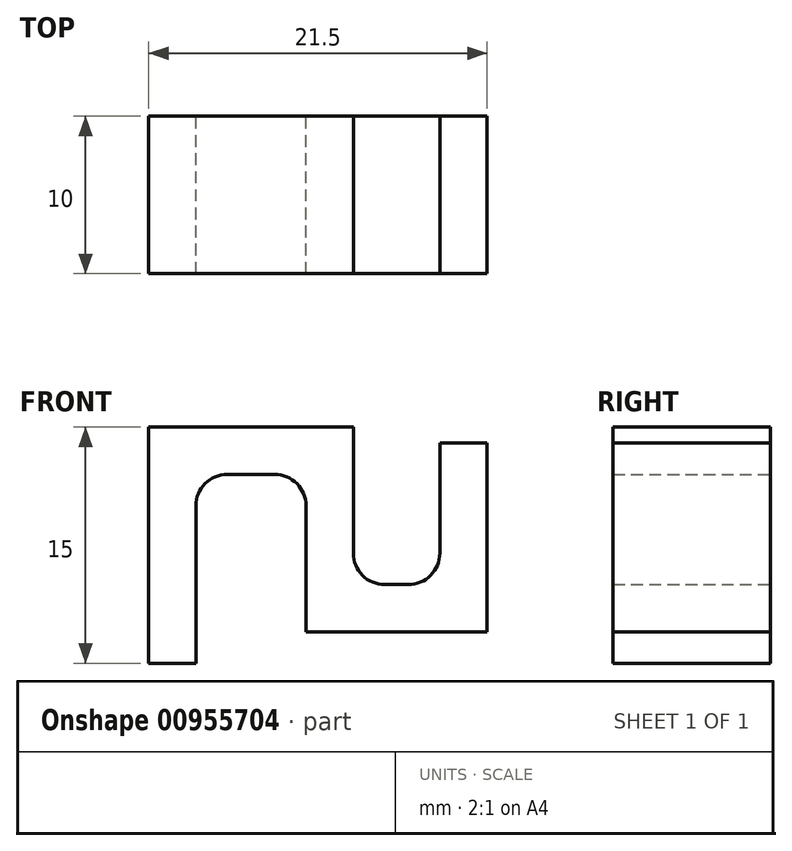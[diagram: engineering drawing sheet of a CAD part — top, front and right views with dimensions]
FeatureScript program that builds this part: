
annotation { "Feature Type Name" : "Feature", "Feature Type Description" : "" }
export const myFeature = defineFeature(function(context is Context, id is Id, definition is map)
    precondition{}
    {
        {
            var Q0;
            Q0=qCreatedBy(makeId("Front.planeOp"),FACE);
            var sketch = newSketch(context, id + "F0", { "sketchPlane" : qUnion([Q0])});
            skLineSegment(sketch, "E0", {"start": v(0, 0) * mm, "end": v(0, 15) * mm});
            skLineSegment(sketch, "E1", {"start": v(0, 15) * mm, "end": v(13, 15) * mm});
            skLineSegment(sketch, "E2", {"start": v(13, 15) * mm, "end": v(13, 7) * mm});
            skLineSegment(sketch, "E3", {"start": v(15, 5) * mm, "end": v(16.5, 5) * mm});
            skLineSegment(sketch, "E4", {"start": v(18.5, 7) * mm, "end": v(18.5, 14) * mm});
            skLineSegment(sketch, "E5", {"start": v(18.5, 14) * mm, "end": v(21.5, 14) * mm});
            skLineSegment(sketch, "E6", {"start": v(21.5, 14) * mm, "end": v(21.5, 2) * mm});
            skLineSegment(sketch, "E7", {"start": v(21.5, 2) * mm, "end": v(10, 2) * mm});
            skLineSegment(sketch, "E8", {"start": v(10, 2) * mm, "end": v(10, 10) * mm});
            skLineSegment(sketch, "E9", {"start": v(8, 12) * mm, "end": v(5, 12) * mm});
            skLineSegment(sketch, "E10", {"start": v(3, 10) * mm, "end": v(3, 0) * mm});
            skLineSegment(sketch, "E11", {"start": v(3, 0) * mm, "end": v(0, 0) * mm});
            skPoint(sketch, "E12.visualSharp", {"position": v(10, 12) * mm});
            skArc(sketch, "E12.filletArc", {"start": v(10, 10) * mm, "mid": v(9.41, 11.41) * mm, "end": v(8, 12) * mm});
            skPoint(sketch, "E13.visualSharp", {"position": v(3, 12) * mm});
            skArc(sketch, "E13.filletArc", {"start": v(5, 12) * mm, "mid": v(3.59, 11.41) * mm, "end": v(3, 10) * mm});
            skPoint(sketch, "E14.visualSharp", {"position": v(13, 5) * mm});
            skArc(sketch, "E14.filletArc", {"start": v(13, 7) * mm, "mid": v(13.59, 5.59) * mm, "end": v(15, 5) * mm});
            skPoint(sketch, "E15.visualSharp", {"position": v(18.5, 5) * mm});
            skArc(sketch, "E15.filletArc", {"start": v(16.5, 5) * mm, "mid": v(17.91, 5.59) * mm, "end": v(18.5, 7) * mm});
            skSolve(sketch);
        }
        {
            var Q0;
            Q0=makeQuery(id+"F0.imprint","IMPRINT",FACE,{"disambiguationData":[TD([[makeQuery(id+"F0.imprint","IMPRINT",EDGE,{"derivedFrom":sQuery(id+"F0.wireOp",EDGE,"E0")}),-1.0]])]});
            extrude(context, id + "F1", {"entities" : qUnion([Q0]), "depth" : 10 * mm, "offsetDistance" : 25 * mm});
        }
    });
